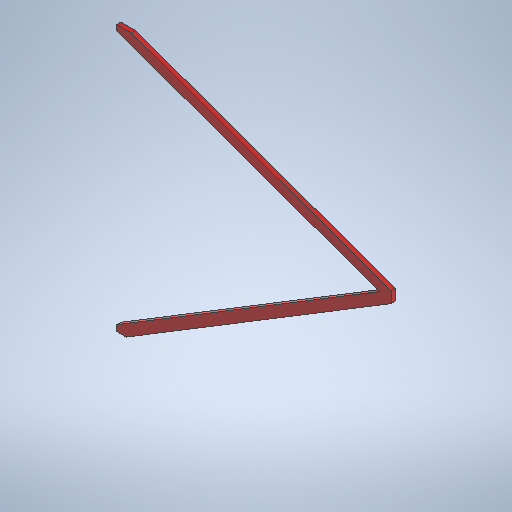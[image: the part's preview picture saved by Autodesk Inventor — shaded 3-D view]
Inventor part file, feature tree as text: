
AUTODESK INVENTOR PART (.ipt)
format: ipt  version: 2025.1 (Build 291241020, 241B)  size: 260,608 bytes
history: native  units: in
note: dims shown in document units (in); Inventor stores cm internally (conversion verified against a paired STEP export)
features: other x7, reference x4, extrude x1, sketch x1
ambient origin geometry x8: Origin, YZ Plane, XZ Plane, XY Plane, X Axis, Y Axis, Z Axis, Center Point
bodies: Solid1 (feature_tree)
feature tree (13):
  extrude  "Extrusion1"  [1 undecoded]
  sketch  "Sketch1"  dims[d0=1.5in d1=0.0in]
  reference  "Reference1"
  reference  "Reference2"
  reference  "Reference3"
  reference  "Reference4"
  other  "<userpath>\Documents\Tburn24\layer1\layer1.iam"
  other  "layer1.iam"
  other  "10'x2x4:1"
  other  "16'x2x4:2"
  other  "10'x2x4:4"
  other  "12'x2x4:1"
  other  "Finish1"
note: 1 required parameter value undecoded (feature->parameter linkage not recoverable at this tier; creation-order binding heuristic only, values carry confidence <= 0.55)
